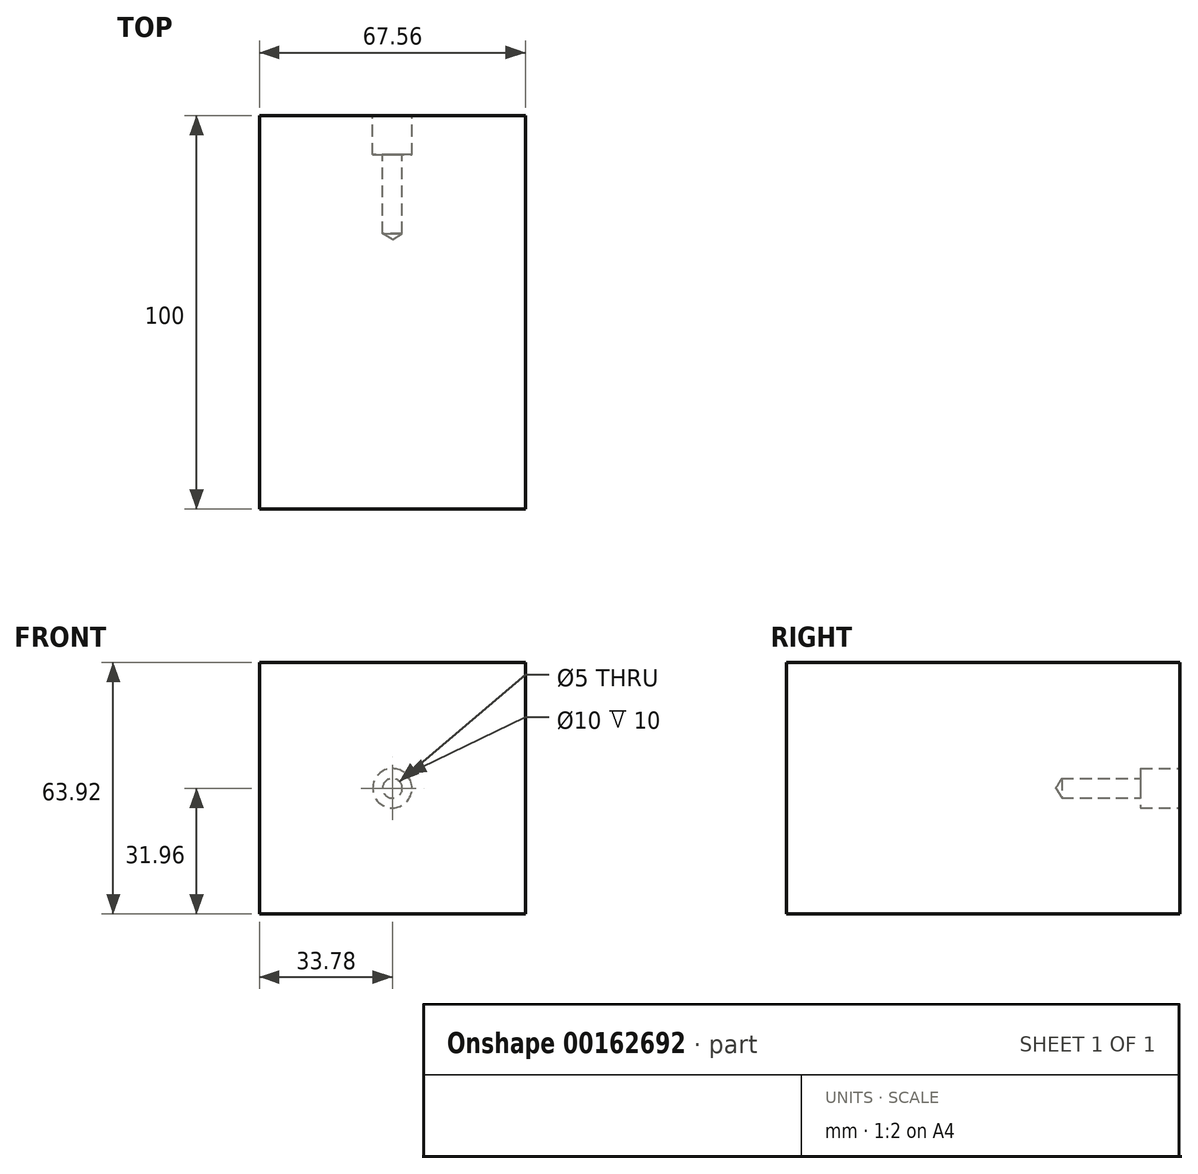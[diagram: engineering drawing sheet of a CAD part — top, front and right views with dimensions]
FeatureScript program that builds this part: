
annotation { "Feature Type Name" : "Feature", "Feature Type Description" : "" }
export const myFeature = defineFeature(function(context is Context, id is Id, definition is map)
    precondition{}
    {
        {
            var Q0;
            Q0=qCreatedBy(makeId("Front.planeOp"),FACE);
            var sketch = newSketch(context, id + "F0", { "sketchPlane" : qUnion([Q0])});
            skLineSegment(sketch, "E0.bottom", {"start": v(33.78, -31.96) * mm, "end": v(-33.78, -31.96) * mm});
            skLineSegment(sketch, "E0.top", {"start": v(33.78, 31.96) * mm, "end": v(-33.78, 31.96) * mm});
            skLineSegment(sketch, "E0.left", {"start": v(33.78, -31.96) * mm, "end": v(33.78, 31.96) * mm});
            skLineSegment(sketch, "E0.right", {"start": v(-33.78, -31.96) * mm, "end": v(-33.78, 31.96) * mm});
            skPoint(sketch, "E0.middle", {"position": v(0, 0) * mm});
            skSolve(sketch);
        }
        {
            var Q0;
            Q0 = qSketchRegion(id + "F0", true);
            extrude(context, id + "F1", {"entities" : qUnion([Q0]), "depth" : 50 * mm});
        }
        {
            var Q0;
            Q0=makeQuery(id+"F1.opExtrude","CAP_FACE",FACE,{"disambiguationData":[OSD([sQuery(id+"F0.wireOp",EDGE,"E0.bottom"),sQuery(id+"F0.wireOp",EDGE,"E0.top"),sQuery(id+"F0.wireOp",EDGE,"E0.left"),sQuery(id+"F0.wireOp",EDGE,"E0.right")])],"isStart":true});
            extrude(context, id + "F2", {"entities" : qUnion([Q0]), "operationType" : NewBodyOperationType.ADD, "depth" : 50 * mm});
        }
        {
            var Q0;
            Q0=makeQuery(id+"F2.opExtrude","CAP_FACE",FACE,{"disambiguationData":[OSD([sQuery(id+"F0.wireOp",EDGE,"E0.bottom"),sQuery(id+"F0.wireOp",EDGE,"E0.top"),sQuery(id+"F0.wireOp",EDGE,"E0.left"),sQuery(id+"F0.wireOp",EDGE,"E0.right")])],"isStart":false});
            var sketch = newSketch(context, id + "F3", { "sketchPlane" : qUnion([Q0])});
            skPoint(sketch, "E1", {"position": v(0, 0) * mm});
            skSolve(sketch);
        }
        {
            var Q0;
            Q0=sQuery(id+"F3.wireOp",VERTEX,"E1");
            var Q1;
            Q1=makeQuery(id+"F1.opExtrude","SWEPT_BODY",BODY,{"disambiguationData":[OSD([sQuery(id+"F0.wireOp",EDGE,"E0.bottom"),sQuery(id+"F0.wireOp",EDGE,"E0.top"),sQuery(id+"F0.wireOp",EDGE,"E0.left"),sQuery(id+"F0.wireOp",EDGE,"E0.right")])]});
            hole(context, id + "F4", {"style" : HoleStyle.C_BORE, "endStyle" : HoleEndStyle.BLIND, "holeDiameter" : 5 * mm, "cBoreDiameter" : 10 * mm, "cBoreDepth" : 10 * mm, "holeDepth" : 30 * mm, "locations" : qUnion([Q0]), "scope" : qUnion([Q1])});
        }
    });
